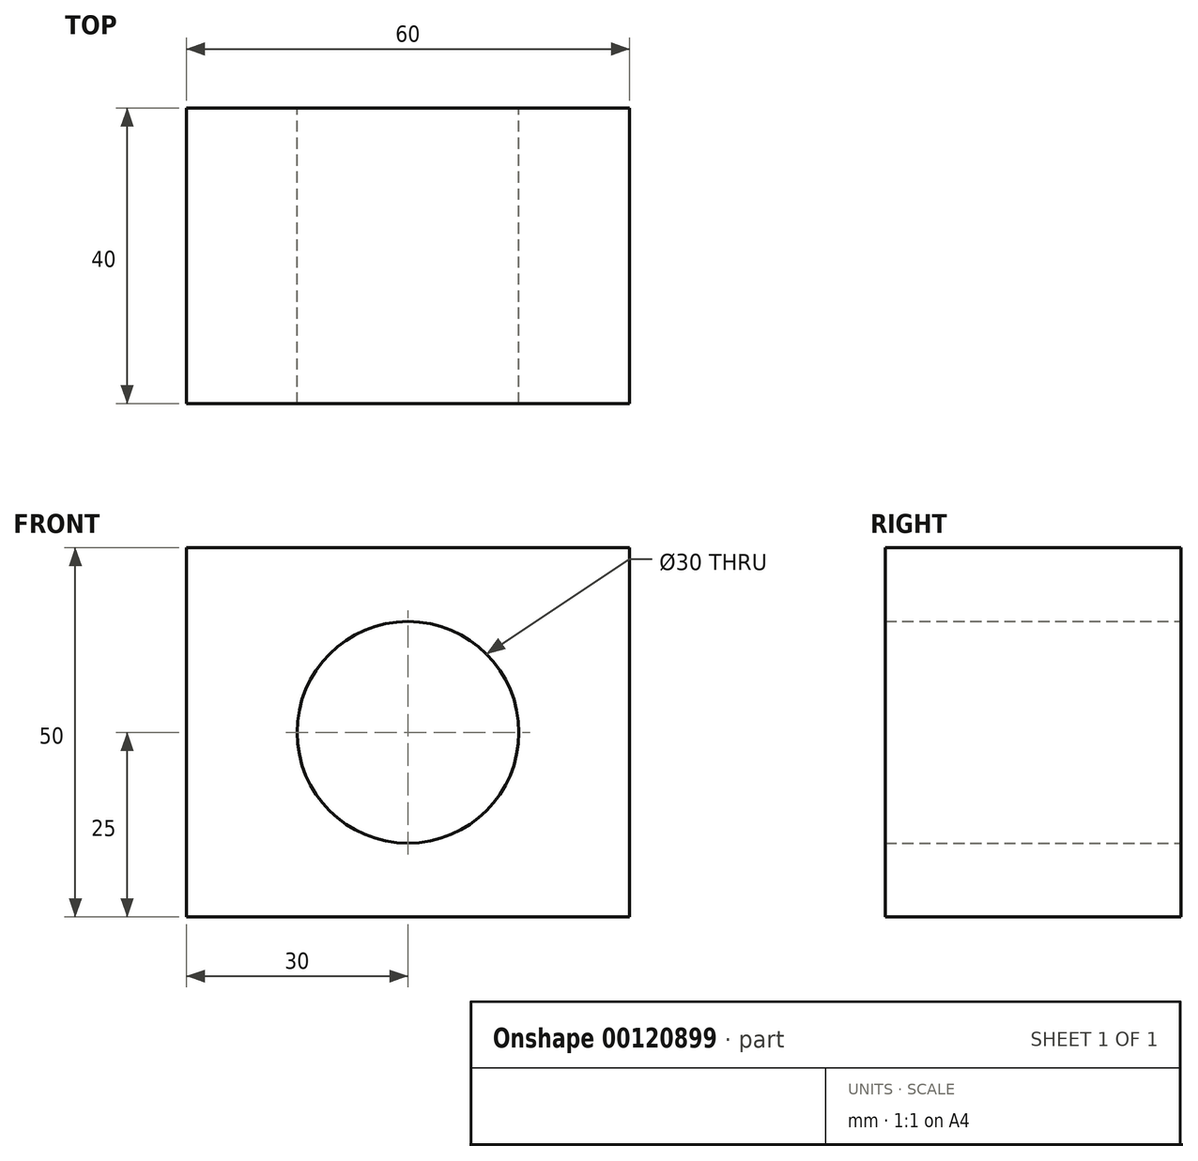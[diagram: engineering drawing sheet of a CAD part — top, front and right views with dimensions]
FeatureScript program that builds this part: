
annotation { "Feature Type Name" : "Feature", "Feature Type Description" : "" }
export const myFeature = defineFeature(function(context is Context, id is Id, definition is map)
    precondition{}
    {
        {
            var Q0;
            Q0=qCreatedBy(makeId("Front.planeOp"),FACE);
            var sketch = newSketch(context, id + "F0", { "sketchPlane" : qUnion([Q0])});
            skLineSegment(sketch, "E0.bottom", {"start": v(-30, 25) * mm, "end": v(30, 25) * mm});
            skLineSegment(sketch, "E0.top", {"start": v(-30, -25) * mm, "end": v(30, -25) * mm});
            skLineSegment(sketch, "E0.left", {"start": v(-30, 25) * mm, "end": v(-30, -25) * mm});
            skLineSegment(sketch, "E0.right", {"start": v(30, 25) * mm, "end": v(30, -25) * mm});
            skPoint(sketch, "E0.middle", {"position": v(0, 0) * mm});
            skCircle(sketch, "E1", {"center": v(0, 0) * mm, "radius": 15 * mm});
            skSolve(sketch);
        }
        {
            var Q0;
            Q0 = qSketchRegion(id + "F0", true);
            extrude(context, id + "F1", {"entities" : qUnion([Q0]), "depth" : 40 * mm});
        }
    });
